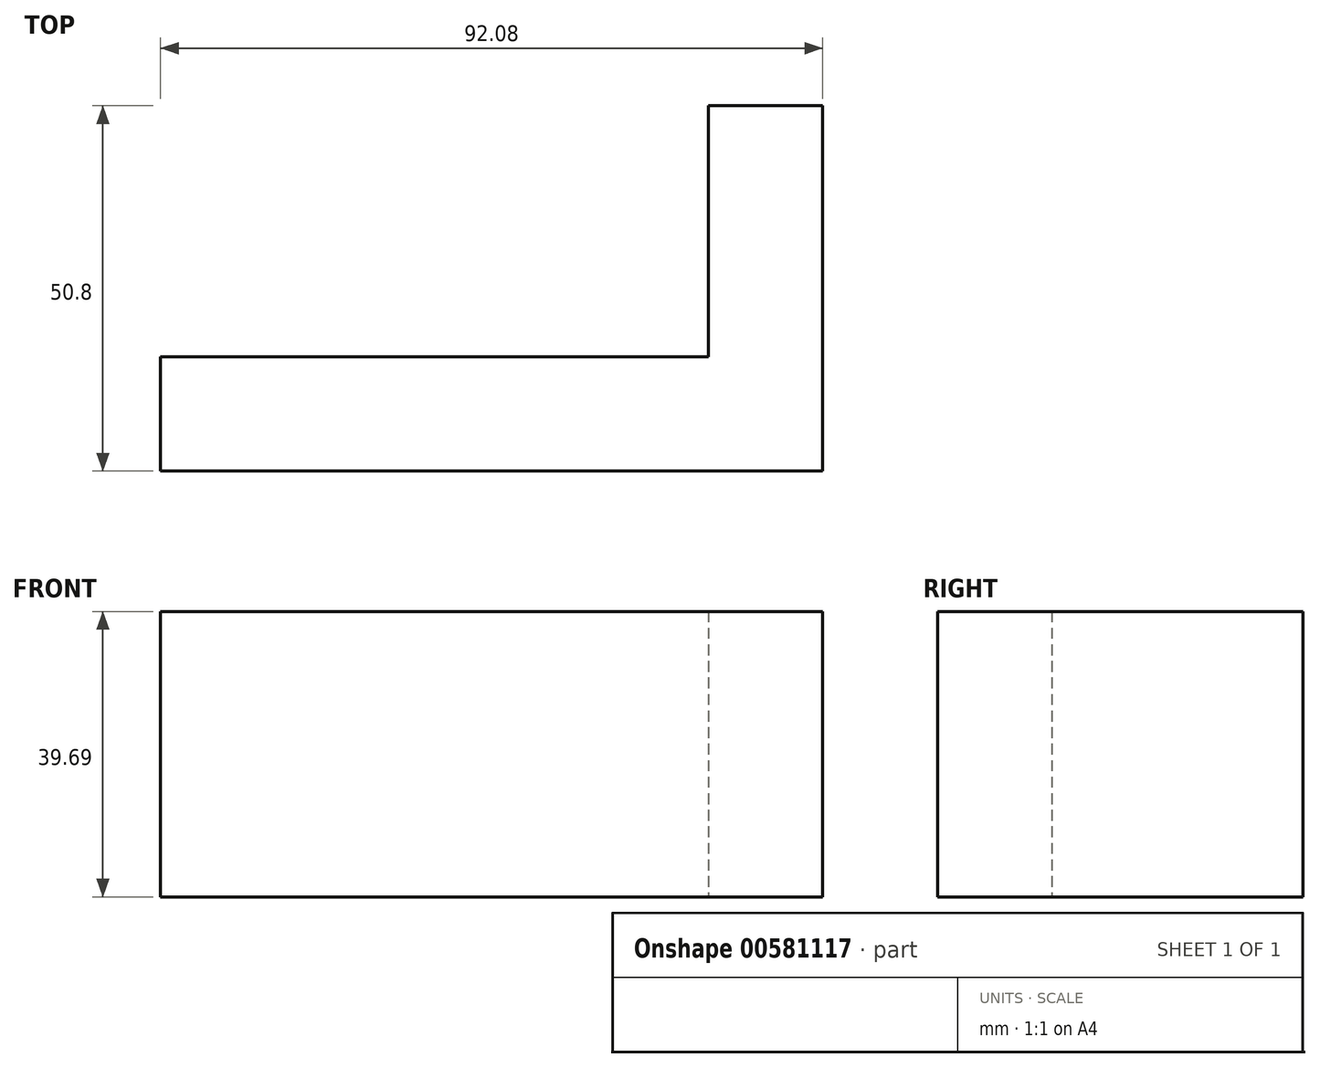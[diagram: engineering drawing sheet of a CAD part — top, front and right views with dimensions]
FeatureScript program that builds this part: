
annotation { "Feature Type Name" : "Feature", "Feature Type Description" : "" }
export const myFeature = defineFeature(function(context is Context, id is Id, definition is map)
    precondition{}
    {
        {
            var Q0;
            Q0=qCreatedBy(makeId("Top.planeOp"),FACE);
            var sketch = newSketch(context, id + "F0", { "sketchPlane" : qUnion([Q0])});
            skLineSegment(sketch, "E0", {"start": v(0, 0) * mm, "end": v(92.08, 0) * mm});
            skLineSegment(sketch, "E1", {"start": v(92.08, 0) * mm, "end": v(92.08, 50.8) * mm});
            skLineSegment(sketch, "E2", {"start": v(92.08, 50.8) * mm, "end": v(76.2, 50.8) * mm});
            skLineSegment(sketch, "E3", {"start": v(76.2, 50.8) * mm, "end": v(76.2, 15.88) * mm});
            skLineSegment(sketch, "E4", {"start": v(76.2, 15.88) * mm, "end": v(0, 15.88) * mm});
            skLineSegment(sketch, "E5", {"start": v(0, 15.88) * mm, "end": v(0, 0) * mm});
            skSolve(sketch);
        }
        {
            var Q0;
            Q0=makeQuery(id+"F0.imprint","IMPRINT",FACE,{"disambiguationData":[TD([[makeQuery(id+"F0.imprint","IMPRINT",EDGE,{"derivedFrom":sQuery(id+"F0.wireOp",EDGE,"E0")}),1.0]])]});
            extrude(context, id + "F1", {"entities" : qUnion([Q0]), "depth" : 39.69 * mm, "offsetDistance" : 25.4 * mm});
        }
    });
